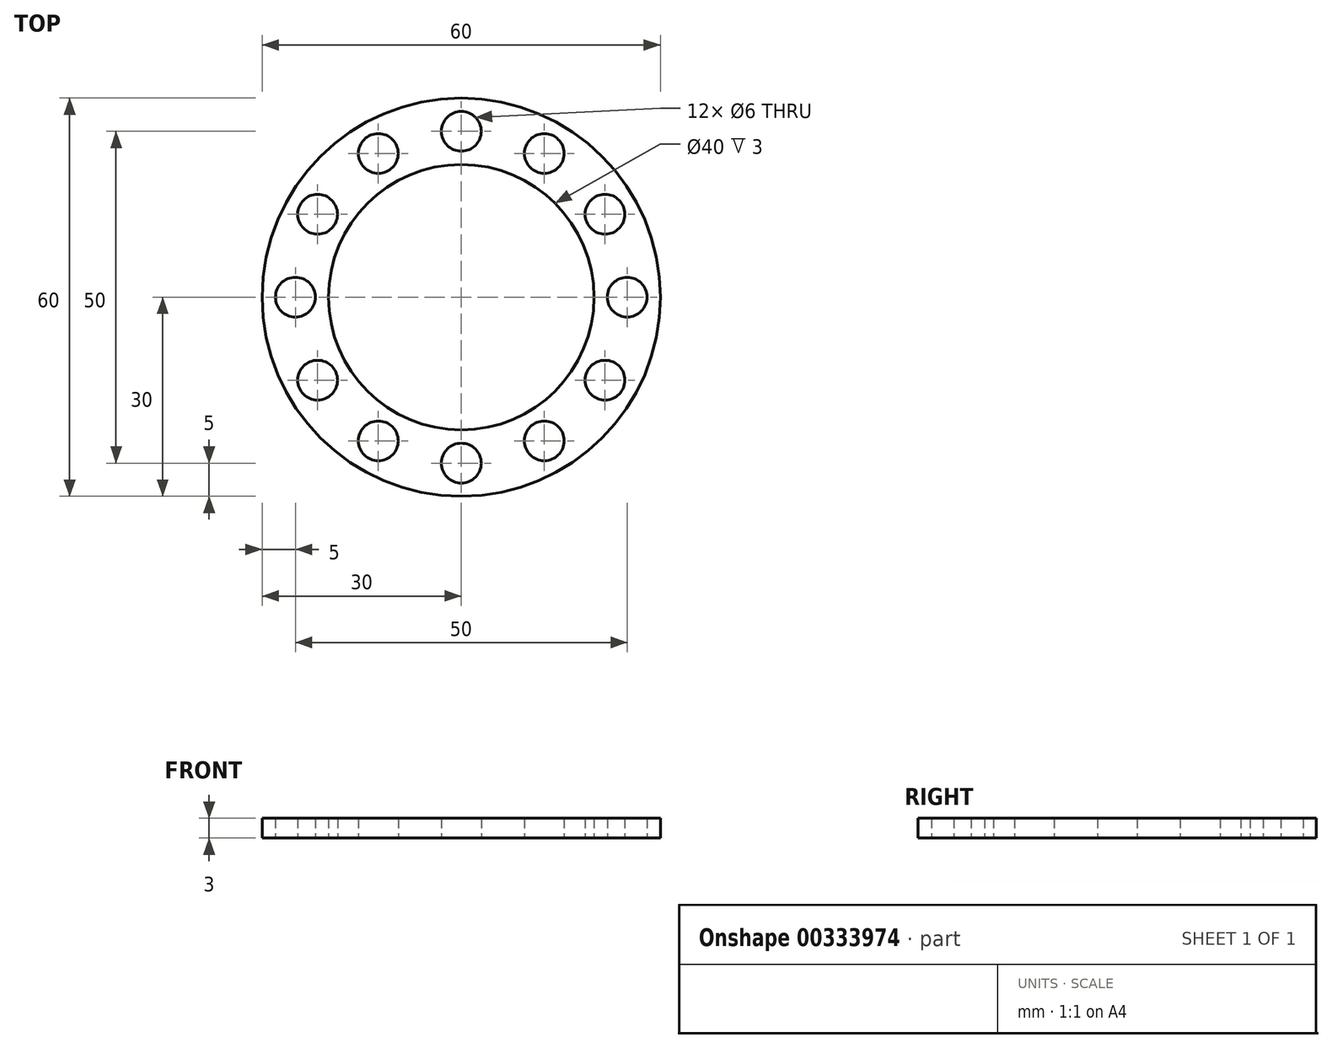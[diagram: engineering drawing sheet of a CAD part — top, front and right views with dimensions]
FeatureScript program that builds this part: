
annotation { "Feature Type Name" : "Feature", "Feature Type Description" : "" }
export const myFeature = defineFeature(function(context is Context, id is Id, definition is map)
    precondition{}
    {
        {
            var Q0;
            Q0=qCreatedBy(makeId("Top.planeOp"),FACE);
            var sketch = newSketch(context, id + "F0", { "sketchPlane" : qUnion([Q0])});
            skCircle(sketch, "E0.cCircle", {"center": v(0, 0) * mm, "radius": 25 * mm, "construction": true});
            skLineSegment(sketch, "E0.0", {"start": v(0, 25) * mm, "end": v(12.5, 21.65) * mm, "construction": true});
            skLineSegment(sketch, "E0.1", {"start": v(12.5, 21.65) * mm, "end": v(21.65, 12.5) * mm, "construction": true});
            skLineSegment(sketch, "E0.2", {"start": v(21.65, 12.5) * mm, "end": v(25, 0) * mm, "construction": true});
            skLineSegment(sketch, "E0.3", {"start": v(25, 0) * mm, "end": v(21.65, -12.5) * mm, "construction": true});
            skLineSegment(sketch, "E0.4", {"start": v(21.65, -12.5) * mm, "end": v(12.5, -21.65) * mm, "construction": true});
            skLineSegment(sketch, "E0.5", {"start": v(12.5, -21.65) * mm, "end": v(0, -25) * mm, "construction": true});
            skLineSegment(sketch, "E0.6", {"start": v(0, -25) * mm, "end": v(-12.5, -21.65) * mm, "construction": true});
            skLineSegment(sketch, "E0.7", {"start": v(-12.5, -21.65) * mm, "end": v(-21.65, -12.5) * mm, "construction": true});
            skLineSegment(sketch, "E0.8", {"start": v(-21.65, -12.5) * mm, "end": v(-25, 0) * mm, "construction": true});
            skLineSegment(sketch, "E0.9", {"start": v(-25, 0) * mm, "end": v(-21.65, 12.5) * mm, "construction": true});
            skLineSegment(sketch, "E0.10", {"start": v(-21.65, 12.5) * mm, "end": v(-12.5, 21.65) * mm, "construction": true});
            skLineSegment(sketch, "E0.11", {"start": v(-12.5, 21.65) * mm, "end": v(0, 25) * mm, "construction": true});
            skCircle(sketch, "E1", {"center": v(-21.65, 12.5) * mm, "radius": 3 * mm});
            skCircle(sketch, "E2", {"center": v(-25, 0) * mm, "radius": 3 * mm});
            skCircle(sketch, "E3", {"center": v(-21.65, -12.5) * mm, "radius": 3 * mm});
            skCircle(sketch, "E4", {"center": v(-12.5, -21.65) * mm, "radius": 3 * mm});
            skCircle(sketch, "E5", {"center": v(0, -25) * mm, "radius": 3 * mm});
            skCircle(sketch, "E6", {"center": v(12.5, -21.65) * mm, "radius": 3 * mm});
            skCircle(sketch, "E7", {"center": v(21.65, -12.5) * mm, "radius": 3 * mm});
            skCircle(sketch, "E8", {"center": v(25, 0) * mm, "radius": 3 * mm});
            skCircle(sketch, "E9", {"center": v(21.65, 12.5) * mm, "radius": 3 * mm});
            skCircle(sketch, "E10", {"center": v(12.5, 21.65) * mm, "radius": 3 * mm});
            skCircle(sketch, "E11", {"center": v(0, 25) * mm, "radius": 3 * mm});
            skCircle(sketch, "E12", {"center": v(-12.5, 21.65) * mm, "radius": 3 * mm});
            skCircle(sketch, "E13", {"center": v(0, 0) * mm, "radius": 20 * mm});
            skCircle(sketch, "E14", {"center": v(0, 0) * mm, "radius": 30 * mm});
            skSolve(sketch);
        }
        {
            var Q0;
            Q0=makeQuery(id+"F0.imprint","IMPRINT",FACE,{"disambiguationData":[TD([[makeQuery(id+"F0.imprint","IMPRINT",EDGE,{"derivedFrom":sQuery(id+"F0.wireOp",EDGE,"E1")}),-1.0]])]});
            extrude(context, id + "F1", {"entities" : qUnion([Q0]), "depth" : 3 * mm});
        }
    });
